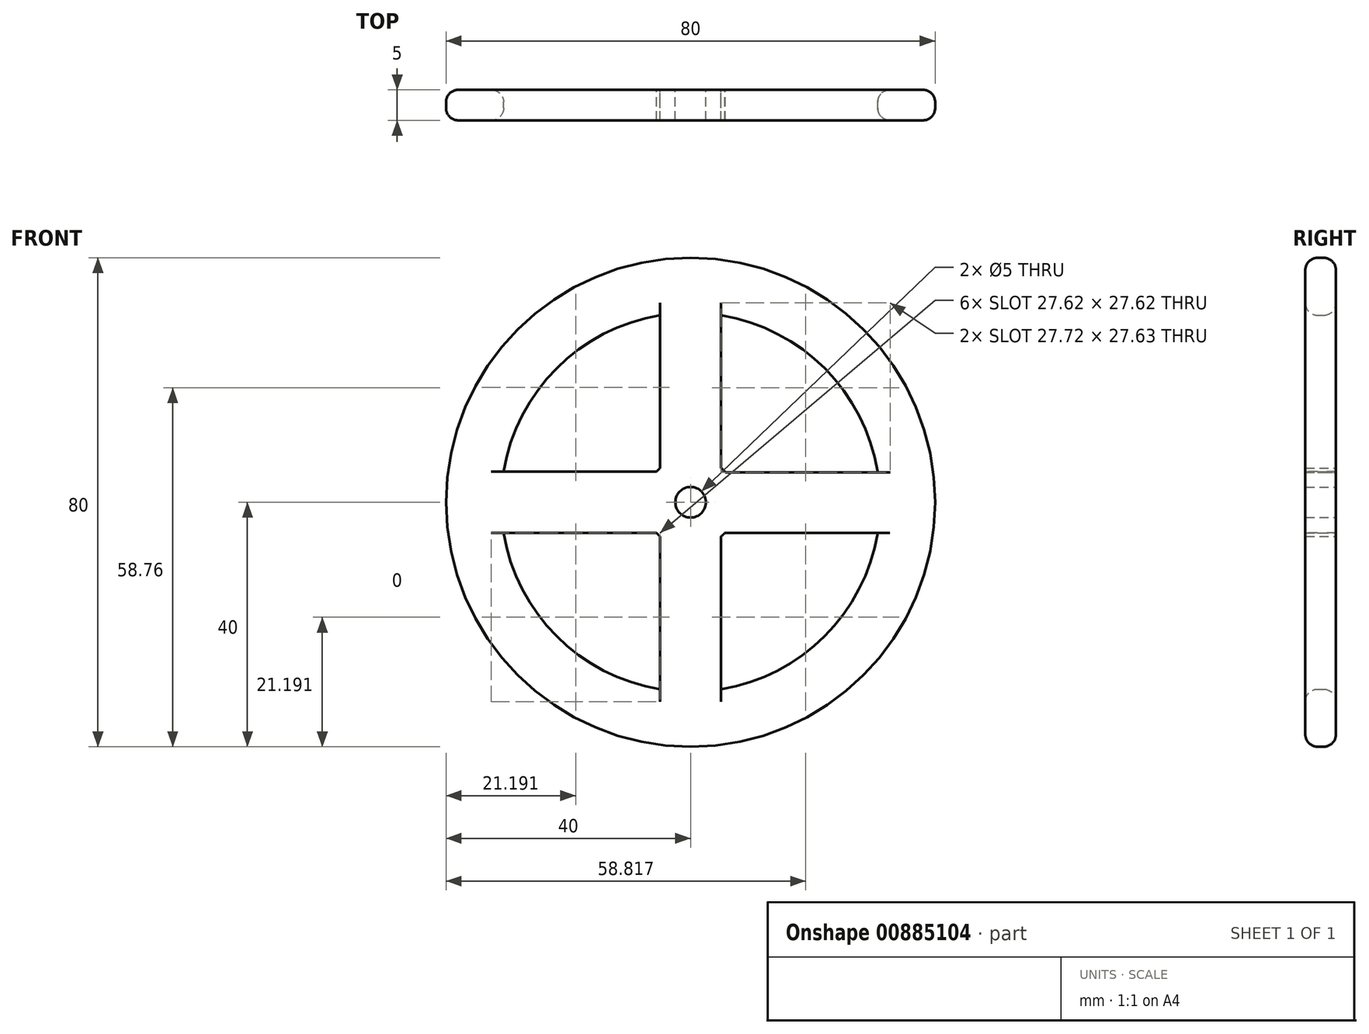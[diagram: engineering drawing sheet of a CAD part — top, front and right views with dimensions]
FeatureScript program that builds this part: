
annotation { "Feature Type Name" : "Feature", "Feature Type Description" : "" }
export const myFeature = defineFeature(function(context is Context, id is Id, definition is map)
    precondition{}
    {
        {
            var Q0;
            Q0=qCreatedBy(makeId("Front.planeOp"),FACE);
            var sketch = newSketch(context, id + "F0", { "sketchPlane" : qUnion([Q0])});
            skCircle(sketch, "E0", {"center": v(0, 0) * mm, "radius": 40 * mm});
            skArc(sketch, "E1", {"start": v(-30.6, -5) * mm, "mid": v(-21.92, -21.92) * mm, "end": v(-5, -30.6) * mm});
            skArc(sketch, "E2", {"start": v(-5, 5.6) * mm, "mid": v(-5.3, 5.3) * mm, "end": v(-5.6, 5) * mm});
            skCircle(sketch, "E3", {"center": v(0, 0) * mm, "radius": 2.5 * mm});
            skLineSegment(sketch, "E4", {"start": v(-7.5, 0) * mm, "end": v(-40, 0) * mm, "construction": true});
            skLineSegment(sketch, "E5", {"start": v(0, -7.5) * mm, "end": v(0, -40) * mm, "construction": true});
            skLineSegment(sketch, "E6", {"start": v(7.5, 0) * mm, "end": v(40, 0) * mm, "construction": true});
            skLineSegment(sketch, "E7", {"start": v(0, 7.5) * mm, "end": v(0, 40) * mm, "construction": true});
            skLineSegment(sketch, "E8.0", {"start": v(5, 5.6) * mm, "end": v(5, 30.6) * mm});
            skLineSegment(sketch, "E9.0", {"start": v(-5, 5.6) * mm, "end": v(-5, 30.6) * mm});
            skLineSegment(sketch, "E10.0", {"start": v(-5.6, 5) * mm, "end": v(-30.6, 5) * mm});
            skLineSegment(sketch, "E11.0", {"start": v(-5, -5.6) * mm, "end": v(-5, -30.6) * mm});
            skLineSegment(sketch, "E12.0", {"start": v(-5.6, -5) * mm, "end": v(-30.6, -5) * mm});
            skLineSegment(sketch, "E13.0", {"start": v(5, -5.6) * mm, "end": v(5, -30.6) * mm});
            skLineSegment(sketch, "E14.0", {"start": v(5.6, -5) * mm, "end": v(30.6, -5) * mm});
            skLineSegment(sketch, "E15.0", {"start": v(5.68, 4.9) * mm, "end": v(30.61, 4.9) * mm});
            skArc(sketch, "E16.trimOffspring", {"start": v(5.68, 4.9) * mm, "mid": v(5.35, 5.26) * mm, "end": v(5, 5.6) * mm});
            skArc(sketch, "E17.trimOffspring", {"start": v(5, -5.6) * mm, "mid": v(5.3, -5.3) * mm, "end": v(5.6, -5) * mm});
            skArc(sketch, "E18.trimOffspring", {"start": v(-5.6, -5) * mm, "mid": v(-5.3, -5.3) * mm, "end": v(-5, -5.6) * mm});
            skArc(sketch, "E19.trimOffspring", {"start": v(5, -30.6) * mm, "mid": v(21.92, -21.92) * mm, "end": v(30.6, -5) * mm});
            skArc(sketch, "E20.trimOffspring", {"start": v(-5, 30.6) * mm, "mid": v(-21.92, 21.92) * mm, "end": v(-30.6, 5) * mm});
            skArc(sketch, "E21.trimOffspring", {"start": v(30.61, 4.9) * mm, "mid": v(21.96, 21.88) * mm, "end": v(5, 30.6) * mm});
            skSolve(sketch);
        }
        {
            var Q0;
            Q0=makeQuery(id+"F0.imprint","IMPRINT",FACE,{"disambiguationData":[TD([[makeQuery(id+"F0.imprint","IMPRINT",EDGE,{"derivedFrom":sQuery(id+"F0.wireOp",EDGE,"E0")}),1.0]])]});
            extrude(context, id + "F1", {"entities" : qUnion([Q0]), "endBound" : BoundingType.SYMMETRIC, "depth" : 5 * mm, "offsetDistance" : 25 * mm});
        }
        {
            var Q0;
            Q0=makeQuery(id+"F1.opExtrude","CAP_EDGE",EDGE,{"disambiguationData":[OSD([sQuery(id+"F0.wireOp",EDGE,"E0")])],"isStart":true});
            var Q1;
            Q1=makeQuery(id+"F1.opExtrude","CAP_EDGE",EDGE,{"disambiguationData":[OSD([sQuery(id+"F0.wireOp",EDGE,"E0")])],"isStart":false});
            var Q2;
            Q2=makeQuery(id+"F1.opExtrude","CAP_EDGE",EDGE,{"disambiguationData":[OSD([sQuery(id+"F0.wireOp",EDGE,"E21.trimOffspring")])],"isStart":true});
            var Q3;
            Q3=makeQuery(id+"F1.opExtrude","CAP_EDGE",EDGE,{"disambiguationData":[OSD([sQuery(id+"F0.wireOp",EDGE,"E20.trimOffspring")])],"isStart":true});
            var Q4;
            Q4=makeQuery(id+"F1.opExtrude","CAP_EDGE",EDGE,{"disambiguationData":[OSD([sQuery(id+"F0.wireOp",EDGE,"E19.trimOffspring")])],"isStart":true});
            var Q5;
            Q5=makeQuery(id+"F1.opExtrude","CAP_EDGE",EDGE,{"disambiguationData":[OSD([sQuery(id+"F0.wireOp",EDGE,"E1")])],"isStart":true});
            var Q6;
            Q6=makeQuery(id+"F1.opExtrude","CAP_EDGE",EDGE,{"disambiguationData":[OSD([sQuery(id+"F0.wireOp",EDGE,"E20.trimOffspring")])],"isStart":false});
            var Q7;
            Q7=makeQuery(id+"F1.opExtrude","CAP_EDGE",EDGE,{"disambiguationData":[OSD([sQuery(id+"F0.wireOp",EDGE,"E1")])],"isStart":false});
            var Q8;
            Q8=makeQuery(id+"F1.opExtrude","CAP_EDGE",EDGE,{"disambiguationData":[OSD([sQuery(id+"F0.wireOp",EDGE,"E19.trimOffspring")])],"isStart":false});
            var Q9;
            Q9=makeQuery(id+"F1.opExtrude","CAP_EDGE",EDGE,{"disambiguationData":[OSD([sQuery(id+"F0.wireOp",EDGE,"E21.trimOffspring")])],"isStart":false});
            fillet(context, id + "F2", {"entities" : qUnion([Q0, Q1, Q2, Q3, Q4, Q5, Q6, Q7, Q8, Q9]), "radius" : 2 * mm, "tangentPropagation" : true, "allowEdgeOverflow" : false});
        }
    });
